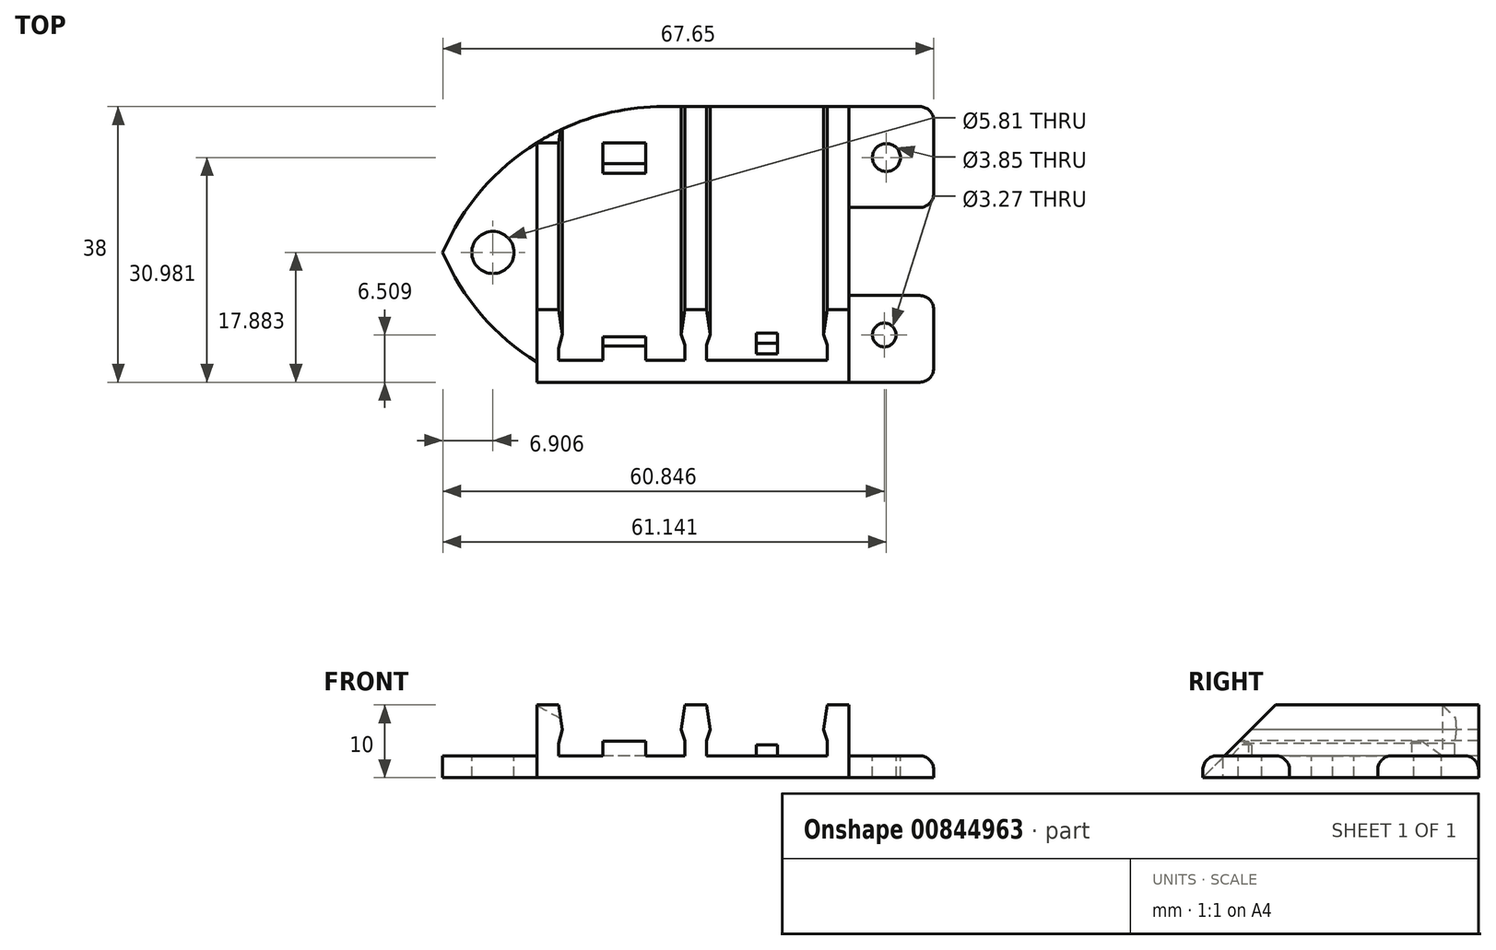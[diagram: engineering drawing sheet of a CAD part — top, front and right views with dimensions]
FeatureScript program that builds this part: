
annotation { "Feature Type Name" : "Feature", "Feature Type Description" : "" }
export const myFeature = defineFeature(function(context is Context, id is Id, definition is map)
    precondition{}
    {
        {
            assignVariable(context, id + "F0", {"name" : "wallthick", "anyValue" : 3});
        }
        {
            var Q0;
            Q0=qCreatedBy(makeId("Top.planeOp"),FACE);
            var sketch = newSketch(context, id + "F1", { "sketchPlane" : qUnion([Q0])});
            skLineSegment(sketch, "E0.bottom", {"start": v(0, 0) * mm, "end": v(43, 0) * mm});
            skLineSegment(sketch, "E0.top", {"start": v(0, -40) * mm, "end": v(43, -40) * mm});
            skLineSegment(sketch, "E0.left", {"start": v(0, 0) * mm, "end": v(0, -40) * mm});
            skLineSegment(sketch, "E0.right", {"start": v(43, 0) * mm, "end": v(43, -40) * mm});
            skSolve(sketch);
        }
        {
            var Q0;
            Q0 = qSketchRegion(id + "F1", true);
            extrude(context, id + "F2", {"entities" : qUnion([Q0]), "depth" : 3 * mm, "offsetDistance" : 25 * mm});
        }
        {
            var Q0;
            Q0=makeQuery(id+"F2.opExtrude","CAP_FACE",FACE,{"disambiguationData":[OSD([sQuery(id+"F1.wireOp",EDGE,"E0.bottom"),sQuery(id+"F1.wireOp",EDGE,"E0.top"),sQuery(id+"F1.wireOp",EDGE,"E0.left"),sQuery(id+"F1.wireOp",EDGE,"E0.right")])],"isStart":false});
            var sketch = newSketch(context, id + "F3", { "sketchPlane" : qUnion([Q0])});
            skLineSegment(sketch, "E1.bottom", {"start": v(0, 0) * mm, "end": v(3, 0) * mm});
            skLineSegment(sketch, "E1.top", {"start": v(0, -40) * mm, "end": v(3, -40) * mm});
            skLineSegment(sketch, "E1.left", {"start": v(0, 0) * mm, "end": v(0, -40) * mm});
            skLineSegment(sketch, "E1.right", {"start": v(3, 0) * mm, "end": v(3, -40) * mm});
            skLineSegment(sketch, "E2.bottom", {"start": v(20.4, 0) * mm, "end": v(23.4, 0) * mm});
            skLineSegment(sketch, "E2.top", {"start": v(20.4, -40) * mm, "end": v(23.4, -40) * mm});
            skLineSegment(sketch, "E2.left", {"start": v(20.4, 0) * mm, "end": v(20.4, -40) * mm});
            skLineSegment(sketch, "E2.right", {"start": v(23.4, 0) * mm, "end": v(23.4, -40) * mm});
            skLineSegment(sketch, "E3.bottom", {"start": v(43, 0) * mm, "end": v(40, 0) * mm});
            skLineSegment(sketch, "E3.top", {"start": v(43, -40) * mm, "end": v(40, -40) * mm});
            skLineSegment(sketch, "E3.left", {"start": v(43, 0) * mm, "end": v(43, -40) * mm});
            skLineSegment(sketch, "E3.right", {"start": v(40, 0) * mm, "end": v(40, -40) * mm});
            skSolve(sketch);
        }
        {
            var Q0;
            Q0 = qSketchRegion(id + "F3", true);
            extrude(context, id + "F4", {"entities" : qUnion([Q0]), "operationType" : NewBodyOperationType.ADD, "depth" : 7 * mm, "offsetDistance" : 25 * mm});
        }
        {
            var Q0;
            Q0=makeQuery(id+"F4.boolean.opBoolean","MERGE",FACE,{"derivedFrom":[makeQuery(id+"F2.opExtrude","SWEPT_FACE",FACE,{"disambiguationData":[OSD([sQuery(id+"F1.wireOp",EDGE,"E0.top")])]}),makeQuery(id+"F4.opExtrude","SWEPT_FACE",FACE,{"disambiguationData":[OSD([sQuery(id+"F3.wireOp",EDGE,"E1.top")])]}),makeQuery(id+"F4.opExtrude","SWEPT_FACE",FACE,{"disambiguationData":[OSD([sQuery(id+"F3.wireOp",EDGE,"E2.top")])]}),makeQuery(id+"F4.opExtrude","SWEPT_FACE",FACE,{"disambiguationData":[OSD([sQuery(id+"F3.wireOp",EDGE,"E3.top")])]})]});
            var sketch = newSketch(context, id + "F5", { "sketchPlane" : qUnion([Q0])});
            skLineSegment(sketch, "E4", {"start": v(3, 10) * mm, "end": v(3.5, 6.6) * mm});
            skLineSegment(sketch, "E5", {"start": v(3.5, 6.6) * mm, "end": v(3, 4.7) * mm});
            skLineSegment(sketch, "E6", {"start": v(20.4, 10) * mm, "end": v(19.9, 6.6) * mm});
            skLineSegment(sketch, "E7", {"start": v(19.9, 6.6) * mm, "end": v(20.4, 5.1) * mm});
            skLineSegment(sketch, "E8", {"start": v(23.4, 10) * mm, "end": v(23.9, 6.6) * mm});
            skPoint(sketch, "E8.endSnap0", {"position": v(23.4, 6.5) * mm});
            skLineSegment(sketch, "E9", {"start": v(23.9, 6.6) * mm, "end": v(23.4, 5.1) * mm});
            skLineSegment(sketch, "E10", {"start": v(0, 5.1) * mm, "end": v(43, 5.1) * mm, "construction": true});
            skLineSegment(sketch, "E11", {"start": v(40, 10) * mm, "end": v(39.5, 6.6) * mm});
            skLineSegment(sketch, "E12", {"start": v(39.5, 6.6) * mm, "end": v(40, 5.1) * mm});
            skLineSegment(sketch, "E13", {"start": v(0, 6.6) * mm, "end": v(43, 6.6) * mm, "construction": true});
            skLineSegment(sketch, "E14", {"start": v(3, 10) * mm, "end": v(3, 4.7) * mm});
            skLineSegment(sketch, "E15", {"start": v(20.4, 10) * mm, "end": v(23.4, 10) * mm});
            skLineSegment(sketch, "E16", {"start": v(23.4, 5.1) * mm, "end": v(20.4, 5.1) * mm});
            skLineSegment(sketch, "E17", {"start": v(40, 10) * mm, "end": v(40, 5.1) * mm});
            skSolve(sketch);
        }
        {
            var Q0;
            Q0 = qSketchRegion(id + "F5", true);
            var Q1;
            Q1=makeQuery(id+"F4.boolean.opBoolean","MERGE",FACE,{"derivedFrom":[makeQuery(id+"F2.opExtrude","SWEPT_FACE",FACE,{"disambiguationData":[OSD([sQuery(id+"F1.wireOp",EDGE,"E0.bottom")])]}),makeQuery(id+"F4.opExtrude","SWEPT_FACE",FACE,{"disambiguationData":[OSD([sQuery(id+"F3.wireOp",EDGE,"E1.bottom")])]}),makeQuery(id+"F4.opExtrude","SWEPT_FACE",FACE,{"disambiguationData":[OSD([sQuery(id+"F3.wireOp",EDGE,"E2.bottom")])]}),makeQuery(id+"F4.opExtrude","SWEPT_FACE",FACE,{"disambiguationData":[OSD([sQuery(id+"F3.wireOp",EDGE,"E3.bottom")])]})]});
            extrude(context, id + "F6", {"entities" : qUnion([Q0]), "operationType" : NewBodyOperationType.ADD, "endBound" : BoundingType.UP_TO_SURFACE, "oppositeDirection" : true, "depth" : 25 * mm, "endBoundEntityFace" : qUnion([Q1]), "offsetDistance" : 25 * mm});
        }
        {
            var Q0;
            {var subQ0=sQuery(id+"F1.wireOp",EDGE,"E0.top");var subQ1=sQuery(id+"F1.wireOp",EDGE,"E0.bottom");Q0=makeQuery(id+"F4.boolean.opBoolean","SPLIT",FACE,{"disambiguationData":[TD([makeQuery(id+"F4.opExtrude","SWEPT_FACE",FACE,{"disambiguationData":[OSD([sQuery(id+"F3.wireOp",EDGE,"E1.right")])]})])],"derivedFrom":makeQuery(id+"F2.opExtrude","CAP_FACE",FACE,{"disambiguationData":[OSD([subQ1,subQ0,sQuery(id+"F1.wireOp",EDGE,"E0.left"),sQuery(id+"F1.wireOp",EDGE,"E0.right")])],"isStart":false})});}
            var sketch = newSketch(context, id + "F7", { "sketchPlane" : qUnion([Q0])});
            skLineSegment(sketch, "E18.bottom", {"start": v(9.07, -40) * mm, "end": v(14.99, -40) * mm});
            skLineSegment(sketch, "E18.top", {"start": v(9.07, -31.73) * mm, "end": v(14.99, -31.73) * mm});
            skLineSegment(sketch, "E18.left", {"start": v(9.07, -40) * mm, "end": v(9.07, -31.73) * mm});
            skLineSegment(sketch, "E18.right", {"start": v(14.99, -40) * mm, "end": v(14.99, -31.73) * mm});
            skLineSegment(sketch, "E19.bottom", {"start": v(9.07, -9.23) * mm, "end": v(14.99, -9.23) * mm});
            skLineSegment(sketch, "E19.top", {"start": v(9.07, -0.83) * mm, "end": v(14.99, -0.83) * mm});
            skLineSegment(sketch, "E19.left", {"start": v(9.07, -9.23) * mm, "end": v(9.07, -0.83) * mm});
            skLineSegment(sketch, "E19.right", {"start": v(14.99, -9.23) * mm, "end": v(14.99, -0.83) * mm});
            skSolve(sketch);
        }
        {
            var Q0;
            Q0 = qSketchRegion(id + "F7", true);
            extrude(context, id + "F8", {"entities" : qUnion([Q0]), "operationType" : NewBodyOperationType.ADD, "depth" : 2 * mm, "offsetDistance" : 25 * mm});
        }
        {
            var Q0;
            Q0=makeQuery(id+"F8.opExtrude","CAP_EDGE",EDGE,{"disambiguationData":[OSD([sQuery(id+"F7.wireOp",EDGE,"E19.top")])],"isStart":false});
            chamfer(context, id + "F9", {"entities" : qUnion([Q0]), "chamferType" : ChamferType.TWO_OFFSETS, "width1" : 5 * mm, "oppositeDirection" : false, "width2" : 7 * mm, "tangentPropagation" : true});
        }
        {
            var Q0;
            Q0=makeQuery(id+"F8.opExtrude","CAP_EDGE",EDGE,{"disambiguationData":[OSD([sQuery(id+"F7.wireOp",EDGE,"E18.bottom")])],"isStart":false});
            chamfer(context, id + "F10", {"entities" : qUnion([Q0]), "width" : 7 * mm, "tangentPropagation" : true});
        }
        {
            var Q0;
            Q0=makeQuery(id+"F4.opExtrude","CAP_EDGE",EDGE,{"disambiguationData":[OSD([sQuery(id+"F3.wireOp",EDGE,"E1.bottom")])],"isStart":false});
            chamfer(context, id + "F11", {"entities" : qUnion([Q0]), "width" : 5 * mm, "tangentPropagation" : true});
        }
        {
            var Q0;
            Q0=makeQuery(id+"F2.opExtrude","CAP_FACE",FACE,{"disambiguationData":[OSD([sQuery(id+"F1.wireOp",EDGE,"E0.bottom"),sQuery(id+"F1.wireOp",EDGE,"E0.top"),sQuery(id+"F1.wireOp",EDGE,"E0.left"),sQuery(id+"F1.wireOp",EDGE,"E0.right")])],"isStart":true});
            var sketch = newSketch(context, id + "F12", { "sketchPlane" : qUnion([Q0])});
            skLineSegment(sketch, "E20.bottom", {"start": v(0, 35.25) * mm, "end": v(-15.62, 35.25) * mm});
            skLineSegment(sketch, "E20.top", {"start": v(0, 0) * mm, "end": v(-15.62, 0) * mm});
            skLineSegment(sketch, "E20.left", {"start": v(0, 38) * mm, "end": v(0, 0) * mm});
            skLineSegment(sketch, "E20.right", {"start": v(-15.62, 35.25) * mm, "end": v(-15.62, 0) * mm});
            skLineSegment(sketch, "E21.bottom", {"start": v(43, 38) * mm, "end": v(54.68, 38) * mm});
            skLineSegment(sketch, "E21.top", {"start": v(43, 26.05) * mm, "end": v(54.68, 26.05) * mm});
            skLineSegment(sketch, "E21.left", {"start": v(43, 38) * mm, "end": v(43, 26.05) * mm});
            skLineSegment(sketch, "E21.right", {"start": v(54.68, 38) * mm, "end": v(54.68, 26.05) * mm});
            skLineSegment(sketch, "E22.bottom", {"start": v(43, 0) * mm, "end": v(54.68, 0) * mm});
            skLineSegment(sketch, "E22.top", {"start": v(43, 13.9) * mm, "end": v(54.68, 13.9) * mm});
            skLineSegment(sketch, "E22.left", {"start": v(43, 0) * mm, "end": v(43, 13.9) * mm});
            skLineSegment(sketch, "E22.right", {"start": v(54.68, 0) * mm, "end": v(54.68, 13.9) * mm});
            skSolve(sketch);
        }
        {
            var Q0;
            Q0 = qSketchRegion(id + "F12", true);
            extrude(context, id + "F13", {"entities" : qUnion([Q0]), "operationType" : NewBodyOperationType.ADD, "oppositeDirection" : true, "depth" : (getVariable(context, 'wallthick')) * mm, "offsetDistance" : 25 * mm});
        }
        {
            var Q0;
            Q0=makeQuery(id+"F13.opExtrude","SWEPT_EDGE",EDGE,{"disambiguationData":[OSD([sQuery(id+"F12.wireOp",EDGE,"E20.bottom"),sQuery(id+"F12.wireOp",EDGE,"E20.right")])]});
            var Q1;
            Q1=makeQuery(id+"F13.opExtrude","SWEPT_EDGE",EDGE,{"disambiguationData":[OSD([sQuery(id+"F12.wireOp",EDGE,"E20.top"),sQuery(id+"F12.wireOp",EDGE,"E20.right")])]});
            fillet(context, id + "F14", {"entities" : qUnion([Q0, Q1]), "radius" : 33.07 * mm, "tangentPropagation" : true, "allowEdgeOverflow" : false});
        }
        {
            var Q0;
            Q0=makeQuery(id+"F13.opExtrude","CAP_FACE",FACE,{"disambiguationData":[OSD([sQuery(id+"F12.wireOp",EDGE,"E20.bottom"),sQuery(id+"F12.wireOp",EDGE,"E20.top"),sQuery(id+"F12.wireOp",EDGE,"E20.left"),sQuery(id+"F12.wireOp",EDGE,"E20.right")])],"isStart":false});
            var sketch = newSketch(context, id + "F15", { "sketchPlane" : qUnion([Q0])});
            skCircle(sketch, "E23", {"center": v(-6.06, -20.12) * mm, "radius": 2.9 * mm});
            skSolve(sketch);
        }
        {
            var Q0;
            Q0 = qSketchRegion(id + "F15", true);
            extrude(context, id + "F16", {"entities" : qUnion([Q0]), "operationType" : NewBodyOperationType.REMOVE, "oppositeDirection" : true, "depth" : 25 * mm, "offsetDistance" : 25 * mm});
        }
        {
            var Q0;
            Q0=makeQuery(id+"F13.opExtrude","CAP_EDGE",EDGE,{"disambiguationData":[OSD([sQuery(id+"F12.wireOp",EDGE,"E21.bottom")])],"isStart":false});
            var Q1;
            Q1=makeQuery(id+"F13.opExtrude","SWEPT_EDGE",EDGE,{"disambiguationData":[OSD([sQuery(id+"F12.wireOp",EDGE,"E21.bottom"),sQuery(id+"F12.wireOp",EDGE,"E21.right")])]});
            var Q2;
            Q2=makeQuery(id+"F13.opExtrude","SWEPT_EDGE",EDGE,{"disambiguationData":[OSD([sQuery(id+"F12.wireOp",EDGE,"E21.top"),sQuery(id+"F12.wireOp",EDGE,"E21.right")])]});
            var Q3;
            Q3=makeQuery(id+"F13.opExtrude","CAP_EDGE",EDGE,{"disambiguationData":[OSD([sQuery(id+"F12.wireOp",EDGE,"E21.top")])],"isStart":false});
            var Q4;
            Q4=makeQuery(id+"F13.opExtrude","SWEPT_EDGE",EDGE,{"disambiguationData":[OSD([sQuery(id+"F12.wireOp",EDGE,"E22.top"),sQuery(id+"F12.wireOp",EDGE,"E22.right")])]});
            var Q5;
            Q5=makeQuery(id+"F13.opExtrude","CAP_EDGE",EDGE,{"disambiguationData":[OSD([sQuery(id+"F12.wireOp",EDGE,"E22.top")])],"isStart":false});
            var Q6;
            Q6=makeQuery(id+"F13.opExtrude","CAP_EDGE",EDGE,{"disambiguationData":[OSD([sQuery(id+"F12.wireOp",EDGE,"E22.right")])],"isStart":false});
            var Q7;
            Q7=makeQuery(id+"F13.opExtrude","CAP_EDGE",EDGE,{"disambiguationData":[OSD([sQuery(id+"F12.wireOp",EDGE,"E22.bottom")])],"isStart":false});
            var Q8;
            Q8=makeQuery(id+"F13.opExtrude","SWEPT_EDGE",EDGE,{"disambiguationData":[OSD([sQuery(id+"F12.wireOp",EDGE,"E22.bottom"),sQuery(id+"F12.wireOp",EDGE,"E22.right")])]});
            var Q9;
            Q9=makeQuery(id+"F13.opExtrude","CAP_EDGE",EDGE,{"disambiguationData":[OSD([sQuery(id+"F12.wireOp",EDGE,"E21.right")])],"isStart":false});
            fillet(context, id + "F17", {"entities" : qUnion([Q0, Q1, Q2, Q3, Q4, Q5, Q6, Q7, Q8, Q9]), "radius" : 1.93 * mm, "tangentPropagation" : true, "allowEdgeOverflow" : false});
        }
        {
            var Q0;
            Q0=makeQuery(id+"F13.opExtrude","CAP_FACE",FACE,{"disambiguationData":[OSD([sQuery(id+"F12.wireOp",EDGE,"E21.bottom"),sQuery(id+"F12.wireOp",EDGE,"E21.top"),sQuery(id+"F12.wireOp",EDGE,"E21.left"),sQuery(id+"F12.wireOp",EDGE,"E21.right")])],"isStart":false});
            var sketch = newSketch(context, id + "F18", { "sketchPlane" : qUnion([Q0])});
            skCircle(sketch, "E24", {"center": v(47.88, -31.5) * mm, "radius": 1.63 * mm});
            skPoint(sketch, "E24.centerSnap0", {"position": v(47.88, -27.98) * mm});
            skPoint(sketch, "E24.centerSnap1", {"position": v(43, -31.5) * mm});
            skCircle(sketch, "E25", {"center": v(48.17, -7.02) * mm, "radius": 1.92 * mm});
            skSolve(sketch);
        }
        {
            var Q0;
            Q0 = qSketchRegion(id + "F18", true);
            extrude(context, id + "F19", {"entities" : qUnion([Q0]), "operationType" : NewBodyOperationType.REMOVE, "oppositeDirection" : true, "depth" : 25 * mm, "offsetDistance" : 25 * mm});
        }
        {
            var Q0;
            {var subQ0=sQuery(id+"F1.wireOp",EDGE,"E0.top");var subQ1=sQuery(id+"F1.wireOp",EDGE,"E0.bottom");Q0=makeQuery(id+"F4.boolean.opBoolean","SPLIT",FACE,{"disambiguationData":[TD([makeQuery(id+"F4.opExtrude","SWEPT_FACE",FACE,{"disambiguationData":[OSD([sQuery(id+"F3.wireOp",EDGE,"E2.right")])]})])],"derivedFrom":makeQuery(id+"F2.opExtrude","CAP_FACE",FACE,{"disambiguationData":[OSD([subQ1,subQ0,sQuery(id+"F1.wireOp",EDGE,"E0.left"),sQuery(id+"F1.wireOp",EDGE,"E0.right")])],"isStart":false})});}
            var sketch = newSketch(context, id + "F20", { "sketchPlane" : qUnion([Q0])});
            skLineSegment(sketch, "E26.bottom", {"start": v(33.17, -31.25) * mm, "end": v(30.23, -31.25) * mm});
            skLineSegment(sketch, "E26.top", {"start": v(33.17, -34.6) * mm, "end": v(30.23, -34.6) * mm});
            skLineSegment(sketch, "E26.left", {"start": v(33.17, -31.25) * mm, "end": v(33.17, -34.6) * mm});
            skLineSegment(sketch, "E26.right", {"start": v(30.23, -31.25) * mm, "end": v(30.23, -34.6) * mm});
            skPoint(sketch, "E26.middle", {"position": v(31.7, -32.93) * mm});
            skPoint(sketch, "E26.middle.positionSnap0", {"position": v(31.7, -35) * mm});
            skPoint(sketch, "E26.centerSnap0", {"position": v(31.7, -35) * mm});
            skSolve(sketch);
        }
        {
            var Q0;
            Q0 = qSketchRegion(id + "F20", true);
            extrude(context, id + "F21", {"entities" : qUnion([Q0]), "operationType" : NewBodyOperationType.ADD, "depth" : 1.5 * mm, "offsetDistance" : 25 * mm});
        }
        {
            var Q0;
            Q0=makeQuery(id+"F21.opExtrude","CAP_EDGE",EDGE,{"disambiguationData":[OSD([sQuery(id+"F20.wireOp",EDGE,"E26.top")])],"isStart":false});
            chamfer(context, id + "F22", {"entities" : qUnion([Q0]), "width" : 2 * mm, "tangentPropagation" : true});
        }
    });
